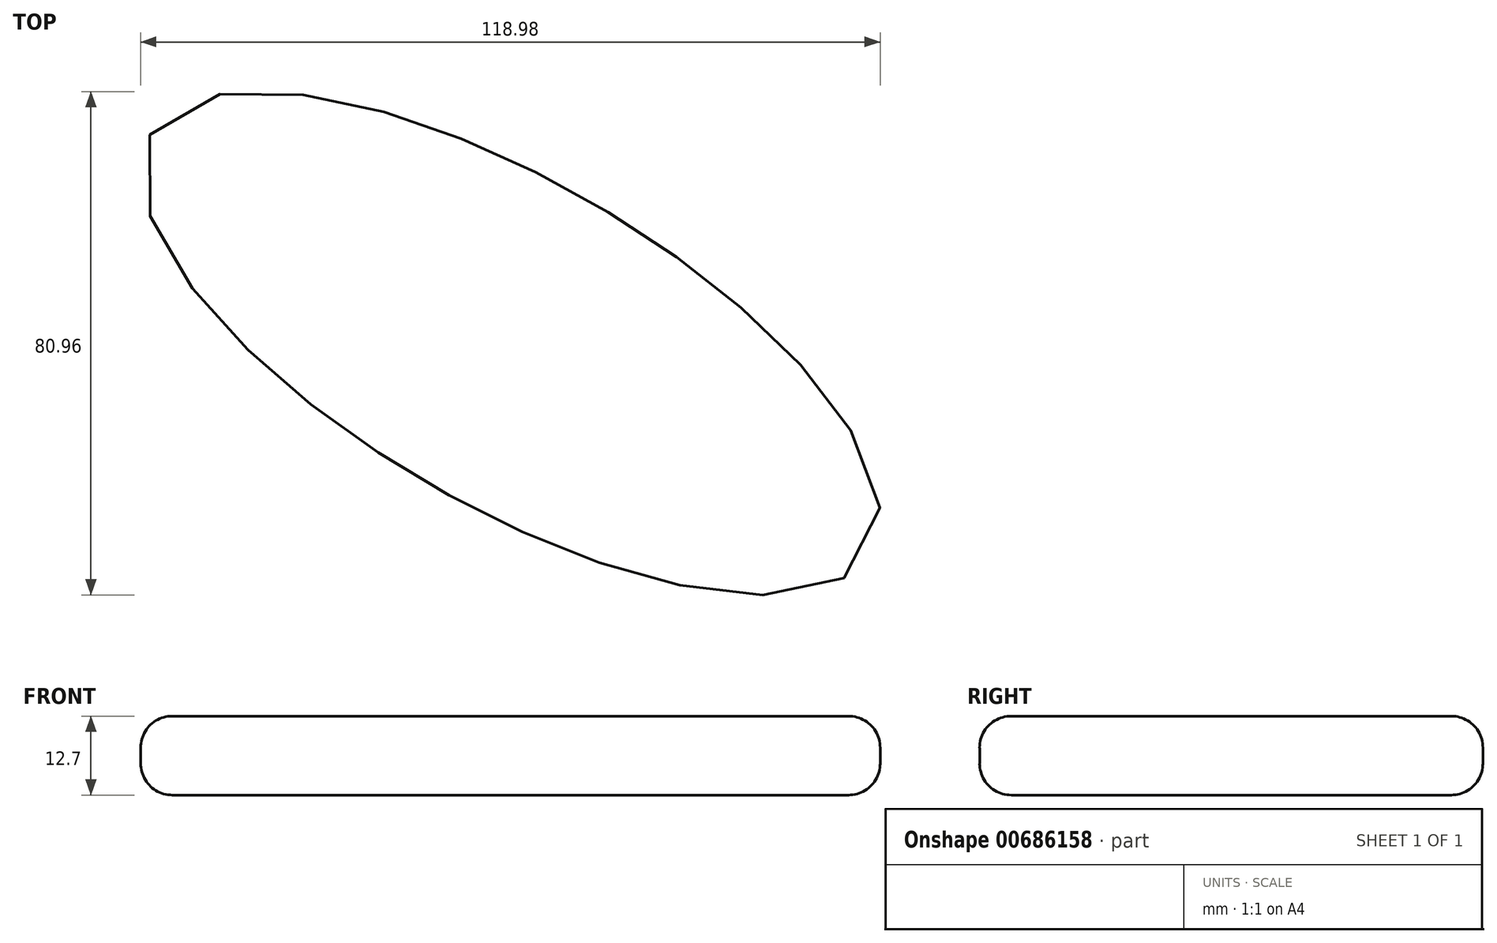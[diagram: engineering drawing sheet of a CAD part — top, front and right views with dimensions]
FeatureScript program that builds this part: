
annotation { "Feature Type Name" : "Feature", "Feature Type Description" : "" }
export const myFeature = defineFeature(function(context is Context, id is Id, definition is map)
    precondition{}
    {
        {
            var Q0;
            Q0=qCreatedBy(makeId("Top.planeOp"),FACE);
            var sketch = newSketch(context, id + "F0", { "sketchPlane" : qUnion([Q0])});
            skEllipse(sketch, "E0", {"center": v(0, 0) * mm, "majorRadius": 67.03 * mm, "minorRadius": 26.16 * mm, "majorAxis": v(-0.87, 0.5)});
            skSolve(sketch);
        }
        {
            var Q0;
            Q0=makeQuery(id+"F0.imprint","IMPRINT",FACE,{"disambiguationData":[TD([[makeQuery(id+"F0.imprint","IMPRINT",EDGE,{"derivedFrom":sQuery(id+"F0.wireOp",EDGE,"E0")}),1.0]])]});
            extrude(context, id + "F1", {"entities" : qUnion([Q0]), "depth" : 12.7 * mm, "offsetDistance" : 25.4 * mm});
        }
        {
            var Q0;
            Q0=makeQuery(id+"F1.opExtrude","CAP_EDGE",EDGE,{"disambiguationData":[OSD([sQuery(id+"F0.wireOp",EDGE,"E0")])],"isStart":false});
            fillet(context, id + "F2", {"entities" : qUnion([Q0]), "radius" : 5.08 * mm, "tangentPropagation" : true, "allowEdgeOverflow" : false});
        }
        {
            var Q0;
            Q0=makeQuery(id+"F1.opExtrude","CAP_FACE",FACE,{"disambiguationData":[OSD([sQuery(id+"F0.wireOp",EDGE,"E0")])],"isStart":true});
            fillet(context, id + "F3", {"entities" : qUnion([Q0]), "radius" : 5.08 * mm, "tangentPropagation" : true, "allowEdgeOverflow" : false});
        }
    });
